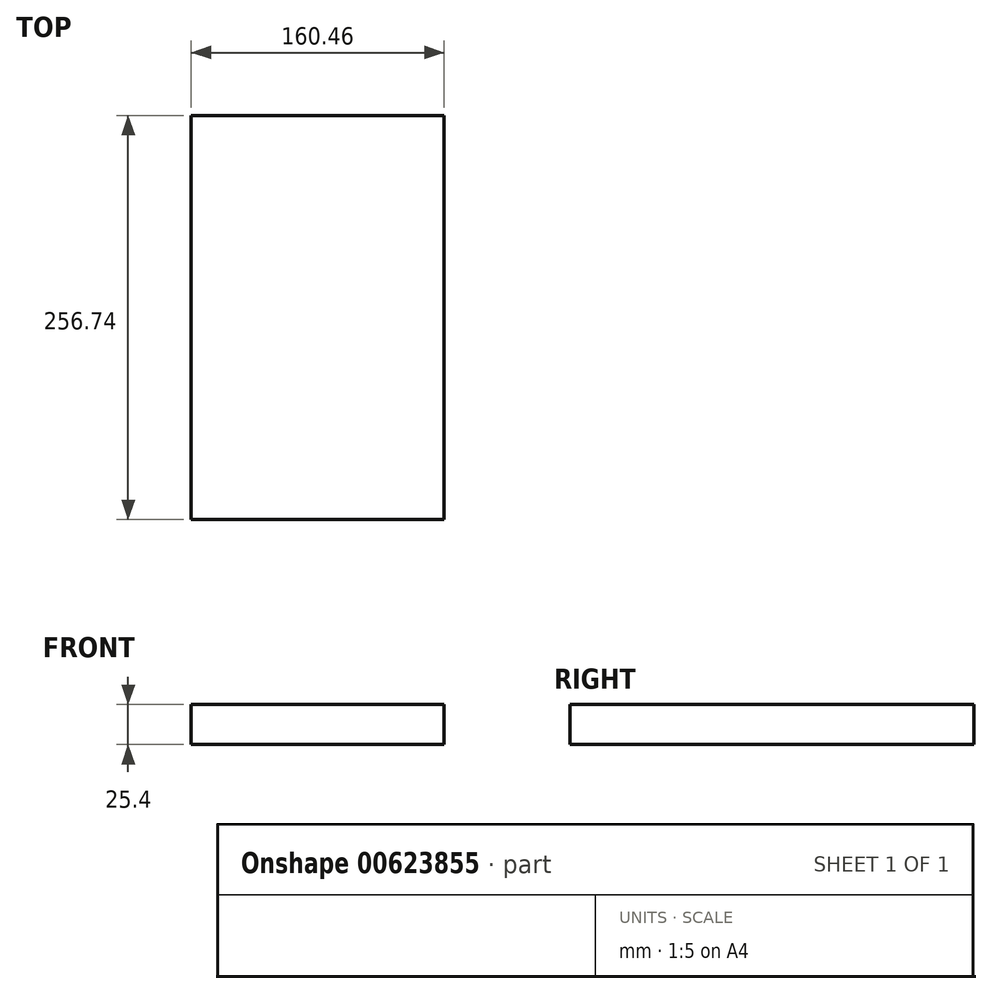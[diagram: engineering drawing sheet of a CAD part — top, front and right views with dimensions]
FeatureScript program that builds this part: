
annotation { "Feature Type Name" : "Feature", "Feature Type Description" : "" }
export const myFeature = defineFeature(function(context is Context, id is Id, definition is map)
    precondition{}
    {
        {
            var Q0;
            Q0=qCreatedBy(makeId("Top.planeOp"),FACE);
            var sketch = newSketch(context, id + "F0", { "sketchPlane" : qUnion([Q0])});
            skLineSegment(sketch, "E0.bottom", {"start": v(-227.64, 131.71) * mm, "end": v(-67.18, 131.71) * mm});
            skLineSegment(sketch, "E0.top", {"start": v(-227.64, -125.03) * mm, "end": v(-67.18, -125.03) * mm});
            skLineSegment(sketch, "E0.left", {"start": v(-227.64, 131.71) * mm, "end": v(-227.64, -125.03) * mm});
            skLineSegment(sketch, "E0.right", {"start": v(-67.18, 131.71) * mm, "end": v(-67.18, -125.03) * mm});
            skSolve(sketch);
        }
        {
            var Q0;
            Q0=makeQuery(id+"F0.imprint","IMPRINT",FACE,{"disambiguationData":[TD([[makeQuery(id+"F0.imprint","IMPRINT",EDGE,{"derivedFrom":sQuery(id+"F0.wireOp",EDGE,"E0.bottom")}),-1.0]])]});
            extrude(context, id + "F1", {"entities" : qUnion([Q0]), "depth" : 25.4 * mm, "offsetDistance" : 25.4 * mm});
        }
    });
